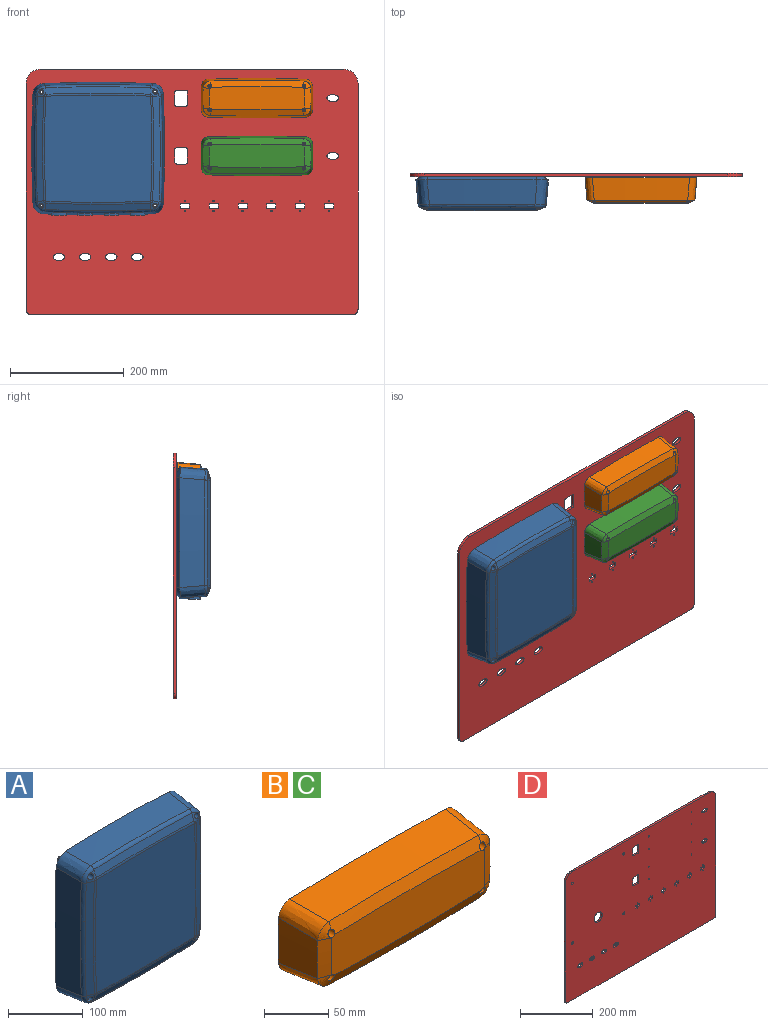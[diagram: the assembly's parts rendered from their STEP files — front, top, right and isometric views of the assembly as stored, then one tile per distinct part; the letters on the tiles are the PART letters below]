
ASSEMBLY  parts=4 mates=3
PART A: 82 faces, bbox 275.9x605.8x275.9 mm
  f0: cone r=2058.99mm half-angle=5deg, axis (0,1,0), area 6594mm2, adj f14,f15,f29,f41,f62,f63,f64,f65
  f1: bspline ~18.84x18.84mm, area 109.5mm2, adj f2,f18,f19,f31,f61
  f2: bspline ~18.67x18.67mm, area 184.5mm2, adj f1,f15,f39,f41,f61
  f3: bspline ~18.84x18.84mm, area 114.2mm2, adj f4,f19,f21,f35,f58
  f4: bspline ~18.67x18.67mm, area 184.5mm2, adj f3,f16,f38,f39,f58
  f5: bspline ~18.84x18.84mm, area 109.5mm2, adj f6,f18,f20,f32,f55
  f6: bspline ~18.67x18.67mm, area 184.5mm2, adj f5,f14,f40,f41,f55
  f7: bspline ~18.84x18.84mm, area 114.2mm2, adj f8,f20,f21,f36,f52
  f8: bspline ~18.67x18.67mm, area 184.5mm2, adj f7,f17,f38,f40,f52
  f9: cone r=2058.99mm half-angle=5deg, axis (0,1,0), area 8319.7mm2, adj f14,f17,f25,f40
  f10: cone r=2058.99mm half-angle=5deg, axis (0,1,0), area 8319.7mm2, adj f15,f16,f26,f39
  f11: cone r=2058.99mm half-angle=5deg, axis (0,1,0), area 8319.7mm2, adj f16,f17,f22,f38
  f12: plane 189.1x189.1mm, normal (0,-1,0), area 35224.7mm2, adj f30,f31,f32,f33,f34,f35,f36,f37
  f13: plane 215.91x215.91mm, normal (0,1,0), area 45558.8mm2, adj f22,f23,f24,f25,f26,f27,f28,f29
  f14: bspline ~605.79x68.9mm, area 1239.8mm2, adj f0,f6,f9,f27,f40,f41
  f15: bspline ~605.79x68.9mm, area 1239.8mm2, adj f0,f2,f10,f28,f39,f41
  f16: bspline ~605.79x68.9mm, area 1239.8mm2, adj f4,f10,f11,f24,f38,f39
  f17: bspline ~605.79x68.9mm, area 1239.8mm2, adj f8,f9,f11,f23,f38,f40
  f18: cone r=2037.83mm half-angle=68.9deg, axis (0,1,0), area 2186.9mm2, adj f1,f5,f30,f41
  f19: cone r=2037.83mm half-angle=68.9deg, axis (0,1,0), area 2186.9mm2, adj f1,f3,f33,f39
  f20: cone r=2037.83mm half-angle=68.9deg, axis (0,1,0), area 2186.9mm2, adj f5,f7,f34,f40
  f21: cone r=2037.83mm half-angle=68.9deg, axis (0,1,0), area 2186.9mm2, adj f3,f7,f37,f38
  f22: cone r=2058.43mm half-angle=54.8deg, axis (0,-1,0), area 2116.7mm2, adj f11,f13,f23,f24
  f23: bspline ~18.49x18.49mm, area 236.8mm2, adj f13,f17,f22,f25,f42
  f24: bspline ~18.49x18.49mm, area 236.8mm2, adj f13,f16,f22,f26,f44
  f25: cone r=2058.43mm half-angle=54.8deg, axis (0,-1,0), area 2116.7mm2, adj f9,f13,f23,f27
  f26: cone r=2058.43mm half-angle=54.8deg, axis (0,-1,0), area 2116.7mm2, adj f10,f13,f24,f28
  f27: bspline ~18.49x18.49mm, area 236.8mm2, adj f13,f14,f25,f29,f46
  f28: bspline ~18.49x18.49mm, area 236.8mm2, adj f13,f15,f26,f29,f48
  f29: cone r=2058.43mm half-angle=54.8deg, axis (0,-1,0), area 2116.7mm2, adj f0,f13,f27,f28
  f30: torus R=2036.06mm, axis (0,-1,0), area 643.1mm2, adj f12,f18,f31,f32
  f31: bspline ~4.45x4.14mm, area 12mm2, adj f1,f12,f30,f33
  f32: bspline ~4.35x4.09mm, area 12mm2, adj f5,f12,f30,f34
  f33: torus R=2036.06mm, axis (0,-1,0), area 642.6mm2, adj f12,f19,f31,f35
  f34: torus R=2036.06mm, axis (0,-1,0), area 643.6mm2, adj f12,f20,f32,f36
  f35: bspline ~4.45x4.14mm, area 12mm2, adj f3,f12,f33,f37
  f36: bspline ~4.35x4.09mm, area 12mm2, adj f7,f12,f34,f37
  f37: torus R=2036.06mm, axis (0,-1,0), area 643.1mm2, adj f12,f21,f35,f36
  f38: torus R=2048.28mm, axis (0,-1,0), area 1313.4mm2, adj f4,f8,f11,f16,f17,f21
  f39: torus R=2048.28mm, axis (0,-1,0), area 1313.4mm2, adj f2,f4,f10,f15,f16,f19
  f40: torus R=2048.28mm, axis (0,-1,0), area 1313.4mm2, adj f6,f8,f9,f14,f17,f20
  f41: torus R=2048.28mm, axis (0,-1,0), area 1313.4mm2, adj f0,f2,f6,f14,f15,f18
  f42: cylinder r=3.97mm len=7.94mm, axis (0,-1,0), area 39.6mm2, adj f13,f23,f43
  f43: plane 7.94x7.94mm, normal (0,1,0), area 31.2mm2, adj f42,f50
  f44: cylinder r=3.97mm len=7.94mm, axis (0,-1,0), area 39.6mm2, adj f13,f24,f45
  f45: plane 7.94x7.94mm, normal (0,1,0), area 31.2mm2, adj f44,f56
  f46: cylinder r=3.97mm len=7.94mm, axis (0,-1,0), area 39.6mm2, adj f13,f27,f47
  f47: plane 7.94x7.94mm, normal (0,1,0), area 31.2mm2, adj f46,f53
  f48: cylinder r=3.97mm len=7.94mm, axis (0,-1,0), area 39.6mm2, adj f13,f28,f49
  f49: plane 7.94x7.94mm, normal (0,1,0), area 31.2mm2, adj f48,f59
  f50: cylinder r=2.41mm len=17.38mm, axis (0,-1,0), area 263.5mm2, adj f43,f51
  f51: plane 8.76x8.76mm, normal (0,-1,0), area 42mm2, adj f50,f52
  f52: cylinder r=4.38mm len=42.13mm, axis (0,-1,0), area 1123.5mm2, adj f7,f8,f51
  f53: cylinder r=2.41mm len=17.38mm, axis (0,-1,0), area 263.5mm2, adj f47,f54
  f54: plane 8.76x8.76mm, normal (0,-1,0), area 42mm2, adj f53,f55
  f55: cylinder r=4.38mm len=42.83mm, axis (0,-1,0), area 1130.8mm2, adj f5,f6,f54
  f56: cylinder r=2.41mm len=17.38mm, axis (0,-1,0), area 263.5mm2, adj f45,f57
  f57: plane 8.76x8.76mm, normal (0,-1,0), area 42mm2, adj f56,f58
  f58: cylinder r=4.38mm len=42.13mm, axis (0,-1,0), area 1123.5mm2, adj f3,f4,f57
  f59: cylinder r=2.41mm len=17.38mm, axis (0,-1,0), area 263.5mm2, adj f49,f60
  f60: plane 8.76x8.76mm, normal (0,-1,0), area 42mm2, adj f59,f61
  f61: cylinder r=4.38mm len=42.83mm, axis (0,-1,0), area 1130.8mm2, adj f1,f2,f60
  f62: cylinder r=38.1mm len=25.4mm, axis (0,0,1), area 122.1mm2, adj f0,f63,f65,f66
  f63: plane 16.91x4.29mm, normal (1,0,0), area 60mm2, adj f0,f62,f64,f66
  f64: cylinder r=38.1mm len=25.4mm, axis (0,0,1), area 83.8mm2, adj f0,f63,f65,f66
  f65: plane 16.91x5.14mm, normal (-1,0,0), area 74.4mm2, adj f0,f62,f64,f66
  f66: plane 25.4x21.27mm, normal (0,0,-1), area 503.9mm2, adj f62,f63,f64,f65
  f67: plane 16.91x3.83mm, normal (-1,0,0), area 52.2mm2, adj f0,f68,f70,f71
  f68: cylinder r=38.1mm len=25.4mm, axis (0,0,1), area 95.4mm2, adj f0,f67,f69,f71
  f69: plane 16.91x3.54mm, normal (1,0,0), area 47.4mm2, adj f0,f68,f70,f71
  f70: cylinder r=38.1mm len=25.4mm, axis (0,0,1), area 57.1mm2, adj f0,f67,f69,f71
  f71: plane 25.4x21.27mm, normal (0,0,-1), area 503.9mm2, adj f67,f68,f69,f70
  f72: plane 16.91x4.29mm, normal (-1,0,0), area 60mm2, adj f0,f73,f75,f76
  f73: cylinder r=38.1mm len=25.4mm, axis (0,0,1), area 122.1mm2, adj f0,f72,f74,f76
  f74: plane 16.91x5.14mm, normal (1,0,0), area 74.4mm2, adj f0,f73,f75,f76
  f75: cylinder r=38.1mm len=25.4mm, axis (0,0,1), area 83.8mm2, adj f0,f72,f74,f76
  f76: plane 25.4x21.27mm, normal (0,0,-1), area 503.9mm2, adj f72,f73,f74,f75
  f77: cylinder r=38.1mm len=25.4mm, axis (0,0,1), area 57.1mm2, adj f0,f78,f80,f81
  f78: plane 16.91x3.54mm, normal (-1,0,0), area 47.4mm2, adj f0,f77,f79,f81
  f79: cylinder r=38.1mm len=25.4mm, axis (0,0,1), area 95.4mm2, adj f0,f78,f80,f81
  f80: plane 16.91x3.83mm, normal (1,0,0), area 52.2mm2, adj f0,f77,f79,f81
  f81: plane 25.4x21.27mm, normal (0,0,-1), area 503.9mm2, adj f77,f78,f79,f80
PART B: 38 faces, bbox 223.7x384.8x96.4 mm
  f0: plane 168.12x41.12mm, normal (0,-1,0), area 6722.9mm2, adj f1,f2,f4,f5,f7,f9,f20,f21
  f1: cone r=2447.87mm half-angle=66.5deg, axis (0,1,0), area 1931.9mm2, adj f0,f2,f7,f12,f31,f37
  f2: bspline ~12.59x12.57mm, area 102.8mm2, adj f0,f1,f17,f20,f37
  f3: cylinder r=4.76mm len=9.53mm, axis (0,-1,0), area 75.7mm2, adj f15,f24,f35
  f4: cone r=2447.87mm half-angle=66.5deg, axis (0,1,0), area 1931.9mm2, adj f0,f5,f9,f14,f28,f34
  f5: bspline ~12.59x12.57mm, area 102.8mm2, adj f0,f4,f18,f20,f34
  f6: cylinder r=4.76mm len=9.53mm, axis (0,-1,0), area 75.7mm2, adj f15,f22,f32
  f7: bspline ~12.59x12.57mm, area 102.8mm2, adj f0,f1,f16,f21,f31
  f8: cylinder r=4.76mm len=9.53mm, axis (0,-1,0), area 75.7mm2, adj f15,f25,f29
  f9: bspline ~12.59x12.57mm, area 102.8mm2, adj f0,f4,f19,f21,f28
  f10: cylinder r=4.76mm len=9.53mm, axis (0,-1,0), area 75.7mm2, adj f15,f23,f26
  f11: cone r=344.2mm half-angle=5deg, axis (0,1,0), area 1582.4mm2, adj f15,f16,f19,f21
  f12: cone r=2462.24mm half-angle=5deg, axis (0,1,0), area 6690.1mm2, adj f1,f15,f16,f17
  f13: cone r=344.2mm half-angle=5deg, axis (0,1,0), area 1582.4mm2, adj f15,f17,f18,f20
  f14: cone r=2462.24mm half-angle=5deg, axis (0,1,0), area 6690.1mm2, adj f4,f15,f18,f19
  f15: plane 197.55x70.55mm, normal (0,1,0), area 12994.6mm2, adj f3,f6,f8,f10,f11,f12,f13,f14
  f16: bspline ~384.12x44.99mm, area 747.5mm2, adj f7,f11,f12,f15
  f17: bspline ~384.12x44.99mm, area 747.5mm2, adj f2,f12,f13,f15
  f18: bspline ~384.12x44.99mm, area 747.5mm2, adj f5,f13,f14,f15
  f19: bspline ~384.12x44.99mm, area 747.5mm2, adj f9,f11,f14,f15
  f20: cone r=329.84mm half-angle=66.5deg, axis (0,1,0), area 423.5mm2, adj f0,f2,f5,f13
  f21: cone r=329.84mm half-angle=66.5deg, axis (0,1,0), area 423.5mm2, adj f0,f7,f9,f11
  f22: plane 9.53x9.53mm, normal (0,1,0), area 70.9mm2, adj f6,f32
  f23: plane 9.53x9.53mm, normal (0,1,0), area 70.9mm2, adj f10,f26
  f24: plane 9.53x9.53mm, normal (0,1,0), area 70.9mm2, adj f3,f35
  f25: plane 9.53x9.53mm, normal (0,1,0), area 70.9mm2, adj f8,f29
  f26: cylinder r=1.75mm len=14.34mm, axis (0,-1,0), area 133.1mm2, adj f10,f15,f23,f27
  f27: plane 6.48x6.48mm, normal (0,-1,0), area 23.3mm2, adj f26,f28
  f28: cylinder r=3.24mm len=32.8mm, axis (0,-1,0), area 644.8mm2, adj f0,f4,f9,f27
  f29: cylinder r=1.75mm len=14.39mm, axis (0,-1,0), area 133.7mm2, adj f8,f15,f25,f30
  f30: plane 6.48x6.48mm, normal (0,-1,0), area 23.3mm2, adj f29,f31
  f31: cylinder r=3.24mm len=32.75mm, axis (0,-1,0), area 643.8mm2, adj f0,f1,f7,f30
  f32: cylinder r=1.75mm len=14.39mm, axis (0,-1,0), area 133.7mm2, adj f6,f15,f22,f33
  f33: plane 6.48x6.48mm, normal (0,-1,0), area 23.3mm2, adj f32,f34
  f34: cylinder r=3.24mm len=32.75mm, axis (0,-1,0), area 643.7mm2, adj f0,f4,f5,f33
  f35: cylinder r=1.75mm len=14.34mm, axis (0,-1,0), area 133.1mm2, adj f3,f15,f24,f36
  f36: plane 6.48x6.48mm, normal (0,-1,0), area 23.3mm2, adj f35,f37
  f37: cylinder r=3.24mm len=32.8mm, axis (0,-1,0), area 644.8mm2, adj f0,f1,f2,f36
PART C: same geometry as B
PART D: 81 faces, bbox 584.2x5.1x431.8 mm
  f0: plane 584.2x431.8mm, normal (0,1,0), area 247588.3mm2, adj f2,f3,f4,f5,f6,f7,f8,f9
  f1: plane 584.2x431.8mm, normal (0,-1,0), area 247588.3mm2, adj f2,f3,f4,f5,f6,f7,f8,f9
  f2: plane 396.88x5.08mm, normal (-1,0,0), area 2016.1mm2, adj f0,f1,f78,f79
  f3: plane 565.15x5.08mm, normal (0,0,-1), area 2871mm2, adj f0,f1,f79,f80
  f4: plane 396.88x5.08mm, normal (1,0,0), area 2016.1mm2, adj f0,f1,f77,f80
  f5: plane 533.4x5.08mm, normal (0,0,1), area 2709.7mm2, adj f0,f1,f77,f78
  f6: plane 15.88x5.08mm, normal (0,0,-1), area 80.6mm2, adj f0,f1,f33,f36
  f7: plane 22.23x5.08mm, normal (1,0,0), area 112.9mm2, adj f0,f1,f35,f36
  f8: plane 15.88x5.08mm, normal (0,0,1), area 80.6mm2, adj f0,f1,f34,f35
  f9: plane 22.23x5.08mm, normal (-1,0,0), area 112.9mm2, adj f0,f1,f33,f34
  f10: plane 22.23x5.08mm, normal (1,0,0), area 112.9mm2, adj f0,f1,f37,f40
  f11: plane 15.88x5.08mm, normal (0,0,1), area 80.6mm2, adj f0,f1,f39,f40
  f12: plane 22.23x5.08mm, normal (-1,0,0), area 112.9mm2, adj f0,f1,f38,f39
  f13: plane 15.88x5.08mm, normal (0,0,-1), area 80.6mm2, adj f0,f1,f37,f38
  f14: cylinder r=3.97mm len=7.94mm, axis (0,-1,0), area 126.7mm2, adj f0,f1
  f15: extruded ~20.34x12.7mm, area 267.2mm2, adj f0,f1
  f16: extruded ~20.34x12.7mm, area 267.2mm2, adj f0,f1
  f17: cylinder r=3.97mm len=7.94mm, axis (0,-1,0), area 126.7mm2, adj f0,f1
  f18: cylinder r=1.75mm len=5.08mm, axis (0,-1,0), area 55.9mm2, adj f0,f1
  f19: cylinder r=1.75mm len=5.08mm, axis (0,-1,0), area 55.9mm2, adj f0,f1
  f20: cylinder r=1.75mm len=5.08mm, axis (0,-1,0), area 55.9mm2, adj f0,f1
  f21: cylinder r=1.75mm len=5.08mm, axis (0,-1,0), area 55.9mm2, adj f0,f1
  f22: cylinder r=3.97mm len=7.94mm, axis (0,-1,0), area 126.7mm2, adj f0,f1
  f23: cylinder r=1.75mm len=5.08mm, axis (0,-1,0), area 55.9mm2, adj f0,f1
  f24: cylinder r=3.97mm len=7.94mm, axis (0,-1,0), area 126.7mm2, adj f0,f1
  f25: cylinder r=15.88mm len=31.75mm, axis (0,-1,0), area 506.7mm2, adj f0,f1
  f26: cylinder r=1.75mm len=5.08mm, axis (0,-1,0), area 55.9mm2, adj f0,f1
  f27: cylinder r=1.75mm len=5.08mm, axis (0,-1,0), area 55.9mm2, adj f0,f1
  f28: cylinder r=1.75mm len=5.08mm, axis (0,-1,0), area 55.9mm2, adj f0,f1
  f29: extruded ~20.34x12.7mm, area 267.2mm2, adj f0,f1
  f30: extruded ~20.34x12.7mm, area 267.2mm2, adj f0,f1
  f31: extruded ~20.34x12.7mm, area 267.2mm2, adj f0,f1
  f32: extruded ~20.34x12.7mm, area 267.2mm2, adj f0,f1
  f33: cylinder r=3.17mm len=5.08mm, axis (0,-1,0), area 25.3mm2, adj f0,f1,f6,f9
  f34: cylinder r=3.17mm len=5.08mm, axis (0,1,0), area 25.3mm2, adj f0,f1,f8,f9
  f35: cylinder r=3.17mm len=5.08mm, axis (0,-1,0), area 25.3mm2, adj f0,f1,f7,f8
  f36: cylinder r=3.17mm len=5.08mm, axis (0,1,0), area 25.3mm2, adj f0,f1,f6,f7
  f37: cylinder r=3.17mm len=5.08mm, axis (0,-1,0), area 25.3mm2, adj f0,f1,f10,f13
  f38: cylinder r=3.17mm len=5.08mm, axis (0,1,0), area 25.3mm2, adj f0,f1,f12,f13
  f39: cylinder r=3.17mm len=5.08mm, axis (0,-1,0), area 25.3mm2, adj f0,f1,f11,f12
  f40: cylinder r=3.17mm len=5.08mm, axis (0,1,0), area 25.3mm2, adj f0,f1,f10,f11
  f41: plane 7.94x5.08mm, normal (1,0,0), area 40.3mm2, adj f0,f1,f42,f44
  f42: plane 15.88x5.08mm, normal (0,0,1), area 80.6mm2, adj f0,f1,f41,f43
  f43: plane 7.94x5.08mm, normal (-1,0,0), area 40.3mm2, adj f0,f1,f42,f44
  f44: plane 15.88x5.08mm, normal (0,0,-1), area 80.6mm2, adj f0,f1,f41,f43
  f45: plane 15.88x5.08mm, normal (0,0,-1), area 80.6mm2, adj f0,f1,f46,f48
  f46: plane 7.94x5.08mm, normal (1,0,0), area 40.3mm2, adj f0,f1,f45,f47
  f47: plane 15.88x5.08mm, normal (0,0,1), area 80.6mm2, adj f0,f1,f46,f48
  f48: plane 7.94x5.08mm, normal (-1,0,0), area 40.3mm2, adj f0,f1,f45,f47
  f49: plane 15.88x5.08mm, normal (0,0,-1), area 80.6mm2, adj f0,f1,f50,f52
  f50: plane 7.94x5.08mm, normal (1,0,0), area 40.3mm2, adj f0,f1,f49,f51
  f51: plane 15.88x5.08mm, normal (0,0,1), area 80.6mm2, adj f0,f1,f50,f52
  f52: plane 7.94x5.08mm, normal (-1,0,0), area 40.3mm2, adj f0,f1,f49,f51
  f53: plane 15.88x5.08mm, normal (0,0,-1), area 80.6mm2, adj f0,f1,f54,f56
  f54: plane 7.94x5.08mm, normal (1,0,0), area 40.3mm2, adj f0,f1,f53,f55
  f55: plane 15.88x5.08mm, normal (0,0,1), area 80.6mm2, adj f0,f1,f54,f56
  f56: plane 7.94x5.08mm, normal (-1,0,0), area 40.3mm2, adj f0,f1,f53,f55
  f57: plane 15.88x5.08mm, normal (0,0,-1), area 80.6mm2, adj f0,f1,f58,f60
  f58: plane 7.94x5.08mm, normal (1,0,0), area 40.3mm2, adj f0,f1,f57,f59
  f59: plane 15.88x5.08mm, normal (0,0,1), area 80.6mm2, adj f0,f1,f58,f60
  f60: plane 7.94x5.08mm, normal (-1,0,0), area 40.3mm2, adj f0,f1,f57,f59
  f61: plane 15.88x5.08mm, normal (0,0,-1), area 80.6mm2, adj f0,f1,f62,f64
  f62: plane 7.94x5.08mm, normal (1,0,0), area 40.3mm2, adj f0,f1,f61,f63
  f63: plane 15.88x5.08mm, normal (0,0,1), area 80.6mm2, adj f0,f1,f62,f64
  f64: plane 7.94x5.08mm, normal (-1,0,0), area 40.3mm2, adj f0,f1,f61,f63
  f65: cylinder r=1.27mm len=5.08mm, axis (0,-1,0), area 40.5mm2, adj f0,f1
  f66: cylinder r=1.27mm len=5.08mm, axis (0,-1,0), area 40.5mm2, adj f0,f1
  f67: cylinder r=1.27mm len=5.08mm, axis (0,-1,0), area 40.5mm2, adj f0,f1
  f68: cylinder r=1.27mm len=5.08mm, axis (0,-1,0), area 40.5mm2, adj f0,f1
  f69: cylinder r=1.27mm len=5.08mm, axis (0,-1,0), area 40.5mm2, adj f0,f1
  f70: cylinder r=1.27mm len=5.08mm, axis (0,-1,0), area 40.5mm2, adj f0,f1
  f71: cylinder r=1.27mm len=5.08mm, axis (0,-1,0), area 40.5mm2, adj f0,f1
  f72: cylinder r=1.27mm len=5.08mm, axis (0,-1,0), area 40.5mm2, adj f0,f1
  f73: cylinder r=1.27mm len=5.08mm, axis (0,-1,0), area 40.5mm2, adj f0,f1
  f74: cylinder r=1.27mm len=5.08mm, axis (0,-1,0), area 40.5mm2, adj f0,f1
  f75: cylinder r=1.27mm len=5.08mm, axis (0,-1,0), area 40.5mm2, adj f0,f1
  f76: cylinder r=1.27mm len=5.08mm, axis (0,-1,0), area 40.5mm2, adj f0,f1
  f77: cylinder r=25.4mm len=25.4mm, axis (0,-1,0), area 202.7mm2, adj f0,f1,f4,f5
  f78: cylinder r=25.4mm len=25.4mm, axis (0,1,0), area 202.7mm2, adj f0,f1,f2,f5
  f79: cylinder r=9.53mm len=9.53mm, axis (0,-1,0), area 76mm2, adj f0,f1,f2,f3
  f80: cylinder r=9.53mm len=9.53mm, axis (0,1,0), area 76mm2, adj f0,f1,f3,f4
PLACE A t=(-165.1,0,76.2)mm
PLACE B t=(323.99,-2.54,35.14)mm
PLACE C t=(323.99,-2.54,-66.46)mm
PLACE D at identity fixed
MATE fastened D.f14 <-> A.f42  axis (0,-1,0) through (-265.1,0,176.2)mm
MATE fastened D.f21 <-> B.f26  axis (0,-1,0) through (31.3,0,186.1)mm
MATE fastened D.f20 <-> C.f26  axis (0,-1,0) through (31.3,0,84.5)mm
